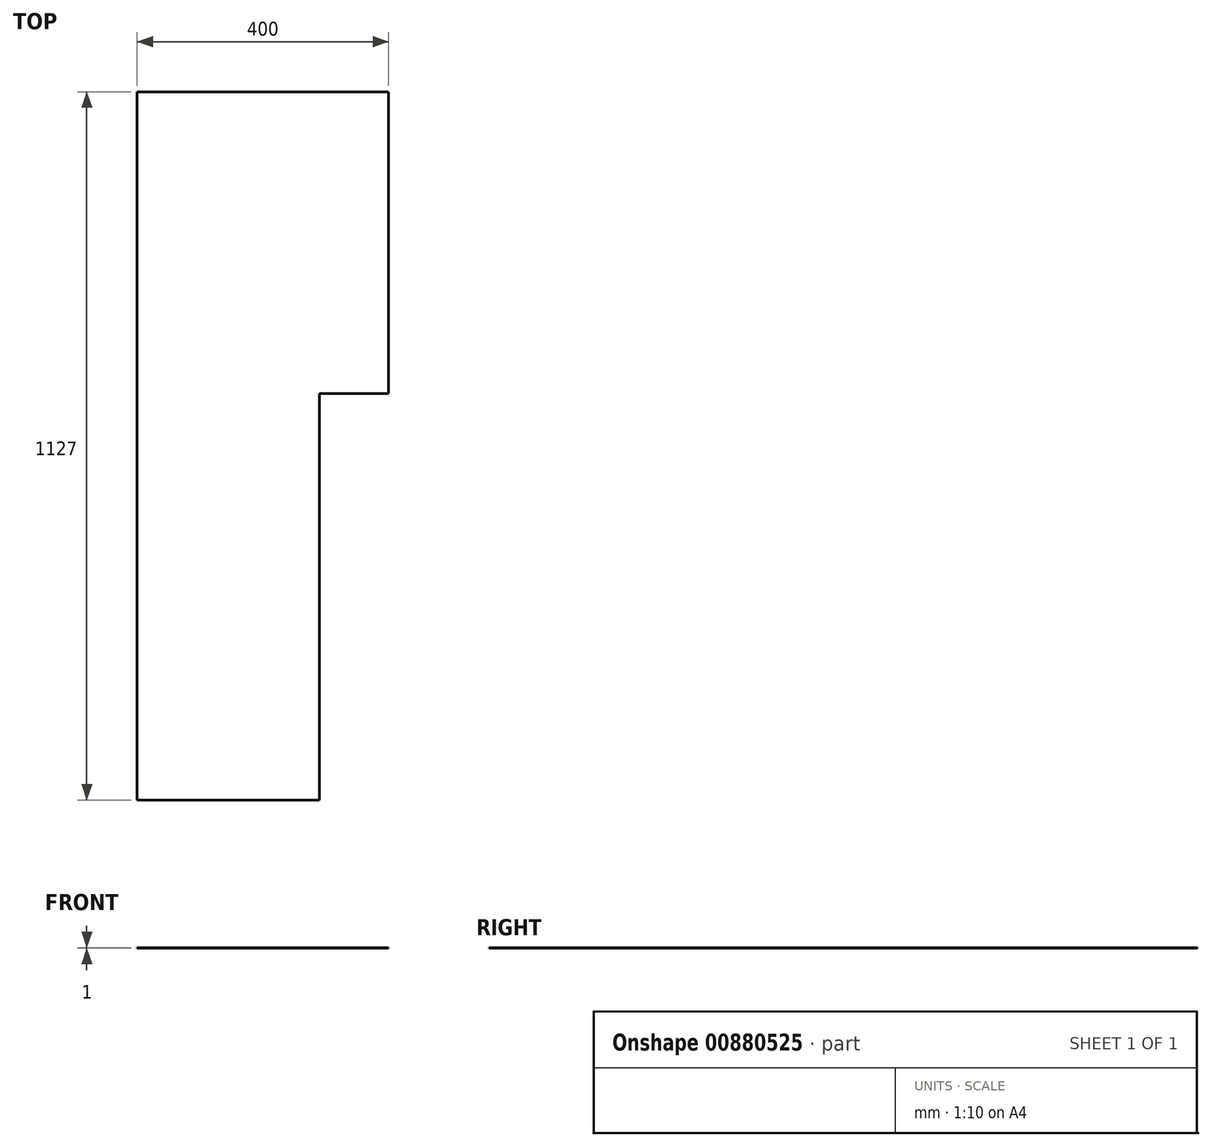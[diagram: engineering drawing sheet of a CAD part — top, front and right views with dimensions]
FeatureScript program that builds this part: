
annotation { "Feature Type Name" : "Feature", "Feature Type Description" : "" }
export const myFeature = defineFeature(function(context is Context, id is Id, definition is map)
    precondition{}
    {
        {
            var Q0;
            Q0=qCreatedBy(makeId("Top.planeOp"),FACE);
            var sketch = newSketch(context, id + "F0", { "sketchPlane" : qUnion([Q0])});
            skLineSegment(sketch, "E0", {"start": v(-363.51, 841.87) * mm, "end": v(36.49, 841.87) * mm});
            skLineSegment(sketch, "E1", {"start": v(36.49, 841.87) * mm, "end": v(36.49, 361.87) * mm});
            skLineSegment(sketch, "E2", {"start": v(36.49, 361.87) * mm, "end": v(-73.51, 361.87) * mm});
            skLineSegment(sketch, "E3", {"start": v(-73.51, 361.87) * mm, "end": v(-73.51, -285.13) * mm});
            skLineSegment(sketch, "E4", {"start": v(-73.51, -285.13) * mm, "end": v(-363.51, -285.13) * mm});
            skLineSegment(sketch, "E5", {"start": v(-363.51, -285.13) * mm, "end": v(-363.51, 841.87) * mm});
            skLineSegment(sketch, "E6", {"start": v(-73.51, 361.87) * mm, "end": v(-363.51, 361.87) * mm});
            skLineSegment(sketch, "E7", {"start": v(-73.51, 59.87) * mm, "end": v(-363.51, 59.87) * mm});
            skLineSegment(sketch, "E8", {"start": v(-193.51, 361.87) * mm, "end": v(-193.51, 59.87) * mm});
            skLineSegment(sketch, "E9", {"start": v(-363.51, 141.87) * mm, "end": v(-193.51, 141.87) * mm});
            skSolve(sketch);
        }
        {
            var Q0;
            {var subQ1=sQuery(id+"F0.wireOp",EDGE,"E0");Q0=makeQuery(id+"F0.imprint","IMPRINT",FACE,{"disambiguationData":[TD([[makeQuery(id+"F0.imprint","IMPRINT",EDGE,{"derivedFrom":subQ1}),-1.0]])]});}
            var Q1;
            {var subQ3=sQuery(id+"F0.wireOp",EDGE,"E9");Q1=makeQuery(id+"F0.imprint","IMPRINT",FACE,{"disambiguationData":[TD([[makeQuery(id+"F0.imprint","IMPRINT",EDGE,{"derivedFrom":subQ3}),1.0]])]});}
            var Q2;
            {var subQ4=sQuery(id+"F0.wireOp",EDGE,"E3");var subQ6=sQuery(id+"F0.wireOp",EDGE,"E7");var subQ7=makeQuery(id+"F0.imprint","INTERSECT",VERTEX,{"derivedFrom":[subQ4,subQ6]});Q2=makeQuery(id+"F0.imprint","IMPRINT",FACE,{"disambiguationData":[TD([[makeQuery(id+"F0.imprint","IMPRINT",EDGE,{"disambiguationData":[TD([[subQ7,-1.0]])],"derivedFrom":subQ6}),-1.0]])]});}
            var Q3;
            {var subQ3=sQuery(id+"F0.wireOp",EDGE,"E9");Q3=makeQuery(id+"F0.imprint","IMPRINT",FACE,{"disambiguationData":[TD([[makeQuery(id+"F0.imprint","IMPRINT",EDGE,{"derivedFrom":subQ3}),-1.0]])]});}
            var Q4;
            {var subQ5=sQuery(id+"F0.wireOp",EDGE,"E4");Q4=makeQuery(id+"F0.imprint","IMPRINT",FACE,{"disambiguationData":[TD([[makeQuery(id+"F0.imprint","IMPRINT",EDGE,{"derivedFrom":subQ5}),-1.0]])]});}
            extrude(context, id + "F1", {"entities" : qUnion([Q0, Q1, Q2, Q3, Q4]), "depth" : 1 * mm, "offsetDistance" : 25 * mm});
        }
    });
